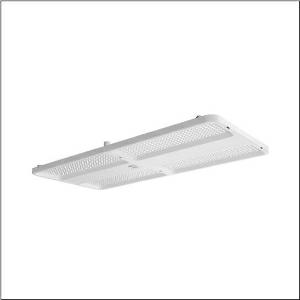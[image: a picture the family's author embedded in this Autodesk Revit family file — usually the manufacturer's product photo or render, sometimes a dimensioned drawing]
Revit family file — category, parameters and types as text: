
# Revit family: highbay_11_maxi_51hn11db4lda01
name_source: partatom
category: Lighting Fixtures
units: mm (PartAtom-declared; Revit-internal decimal feet)

## family parameters
Cut with Voids When Loaded = No
Host = Face
Light Source = No
Part Type = Normal
Room Calculation Point = No
Round Connector Dimension = Use Diameter
Shared = No

## types (1)
- --- (1 x LED, 26000 lm, 125.9 W, 4000K)
    Apparent Load = 126 VA
    CIE Flux Codes = 85 97 100 100 100
    Color Rendering = 80
    Color Temperature = 4000K
    Default Elevation = 1800 mm
    Description = high bay luminaire Highbay 11 maxi; direct symmetric narrow distribution, light control with lens of PMMA; UGR ≤ 19 (X = 4H | Y = 8H | S = 0.25H | reflection values 70/50/20); luminous flux: 26.000lm; light colour: 840, colour temperature: 4000K, MacAdam ≤ 2 SDCM (initial), colour rendering: CRI > 80; luminous efficacy: 206,5lm/W; rated service life: 100.000h (L95/B50) at AT= 25°C; control: Bluetooth® Mesh; for wireless networking: Node multi-sensor luminaire for setting up a local control solution without a higher-level application controller, intelligence completely integrated into the luminaire; with auto-swarm function: leading lighting creates safety. The function is already active without any „out-of-the-box“ commissioning; commissioning is not necessary thanks to „out-of-the-box“ functions: basic functions (presence lighting, follow-up times, fading times, etc.) are already preset at the factory; no control line such as DALI between the Node multi-sensor luminaires and Nodes is required, wireless integration of other Node luminaires and Node multi-sensor luminaires into the network is possible; number of Node multi-sensor luminaires in the project can be expanded as required, network sizes > 300 Nodes can be realized; can also be connected to lighting or building automation via various gateways upon request; integrated DALI2 ECG provides luminaire data (according to IEC62386, Part 251), energy data (Part 252), and monitoring and analytics data (Part 253) to higher-level systems for further processing; luminaire with PIR sensor (passive-infrared); with light sensor; luminaire connection: terminal, 5-pole, max. 2.5mm² (cable entry for one cable, Ø 8.5..16mm); mains connection: 230..240V, AC 50/60Hz; connected load: 125,9W; protection rating (complete): IP65; insulation class (complete): insulation class I (protective earthing); protection symbol: D; certification: CE, ENEC, VDE, UKCA; internal wiring halogen-free; luminaire corresponds to IFS (International Featured Standards) requirements for safety and quality in the food industry; LABS conformity tested according to VDMA 24364:2018-05; housing frame of high-performance plastic PA6, matt traffic white (RAL 9016); cover of PMMA; dimension (LxWxH): 946 x 442 x 72mm; permissible operating ambient temperature: -20..+45°C (reducing of maximum allowable ambient temperature of 5°C with ceiling mounting); packaging unit: 1 piece; (delivery without accessories; please order mounting accessories separately)
    Height = 72 mm  [stored 0.23622 ft]
    Lamp = 1 x LED
    Lamp Light Flux = 26000 lm
    Lamp Power = 125.9 W
    Lamp count = 1
    Length = 946 mm
    Luminous efficacy = 207 lm/W
    Manufacturer = Siteco
    ModVariant = No
    Model = 51HN11DB4LDA01
    Mounting Place = Ceiling
    Mounting Type = Pendant
    Number of Poles = 1
    OnlyDefault = Yes
    Power Factor = 1
    Product Name = Highbay 11 maxi
    Product group = high bay luminaire
    ProductGroupID = 901
    Protection Class = Protection class I
    Protection Degree = IP 65
    RLX_Detail_Level = 1
    RLX_Emergency_Light_Flux = 0 lm
    RLX_Emergency_Type = 0
    RLX_Emergency_Type_DB = No
    RlxData = <blob elided: 127709 chars, md5=b836a63f>
    Socket = socket
    Standby Power = 0 W
    System Light Flux = 26000 lm
    System Power = 126 W
    Type Comments = factory setting: luminous flux: 100 % | dim-lin: 254 | 584 mA
    Type Image = l_1363267.jpg
    URL = http://relux.com
    VarID = @adj_022797
    Voltage = 0 V
    Weight = 0.00 kg
    Width = 442 mm

note: [stored X ft] marks values corroborated as IEEE doubles in the binary element streams (Revit-internal decimal feet)

## geometry (parser evidence)
native form markers: Blend x4, Sweep x10
no freeform markers — native parametric forms only
